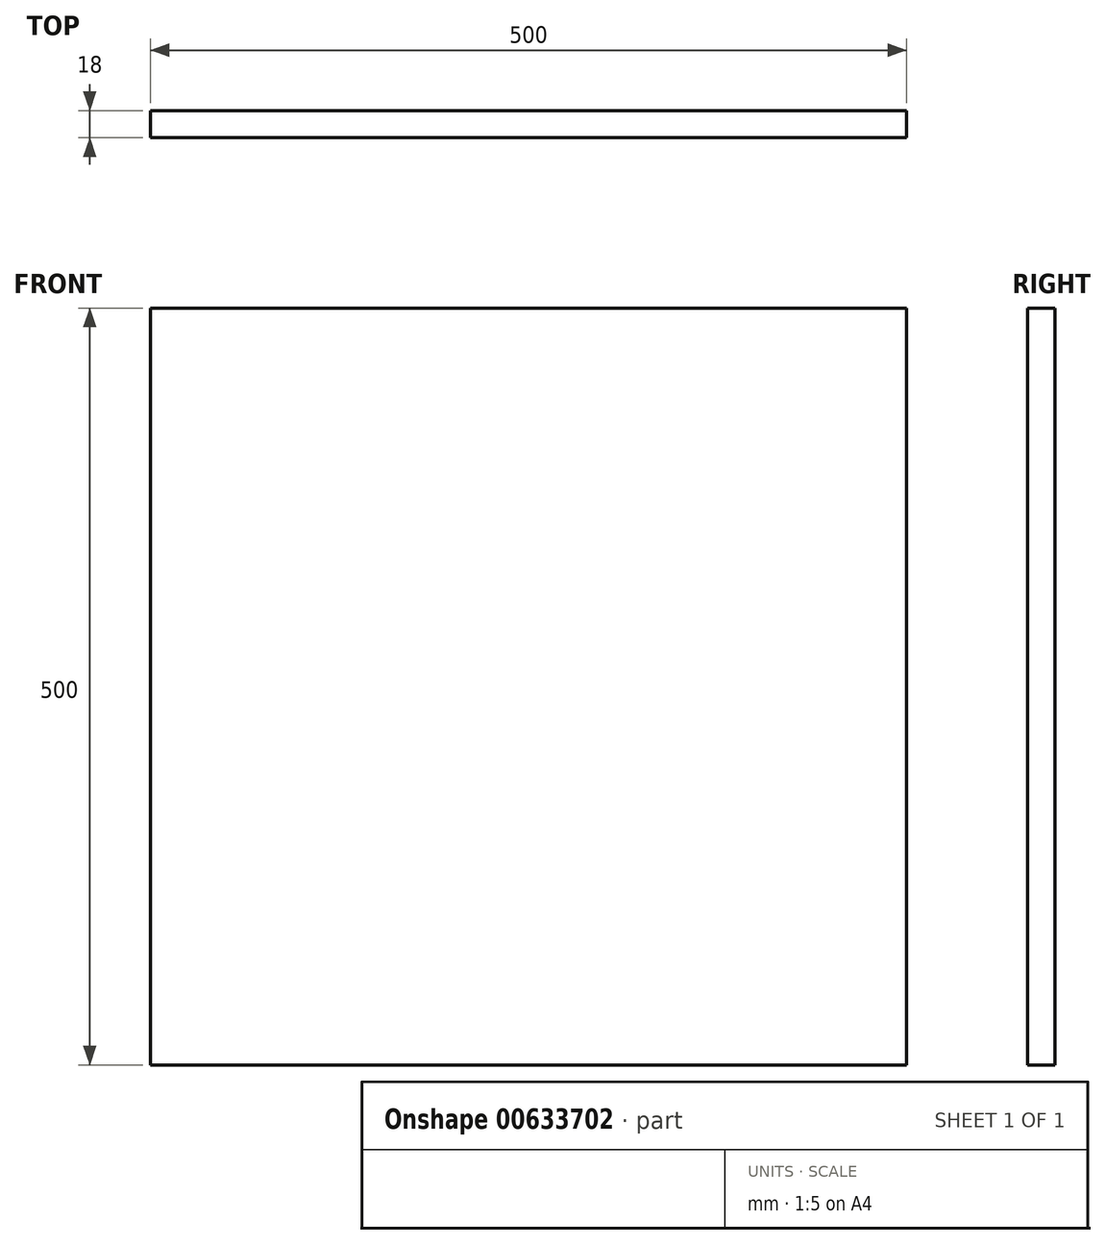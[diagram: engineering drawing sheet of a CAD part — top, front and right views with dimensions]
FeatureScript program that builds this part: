
annotation { "Feature Type Name" : "Feature", "Feature Type Description" : "" }
export const myFeature = defineFeature(function(context is Context, id is Id, definition is map)
    precondition{}
    {
        {
            var Q0;
            Q0=qCreatedBy(makeId("Front.planeOp"),FACE);
            var sketch = newSketch(context, id + "F0", { "sketchPlane" : qUnion([Q0])});
            skLineSegment(sketch, "E0.bottom", {"start": v(-250, 250) * mm, "end": v(250, 250) * mm});
            skLineSegment(sketch, "E0.top", {"start": v(-250, -250) * mm, "end": v(250, -250) * mm});
            skLineSegment(sketch, "E0.left", {"start": v(-250, 250) * mm, "end": v(-250, -250) * mm});
            skLineSegment(sketch, "E0.right", {"start": v(250, 250) * mm, "end": v(250, -250) * mm});
            skPoint(sketch, "E0.middle", {"position": v(0, 0) * mm});
            skSolve(sketch);
        }
        {
            var Q0;
            Q0 = qSketchRegion(id + "F0", true);
            extrude(context, id + "F1", {"entities" : qUnion([Q0]), "depth" : 18 * mm, "offsetDistance" : 25 * mm});
        }
    });
